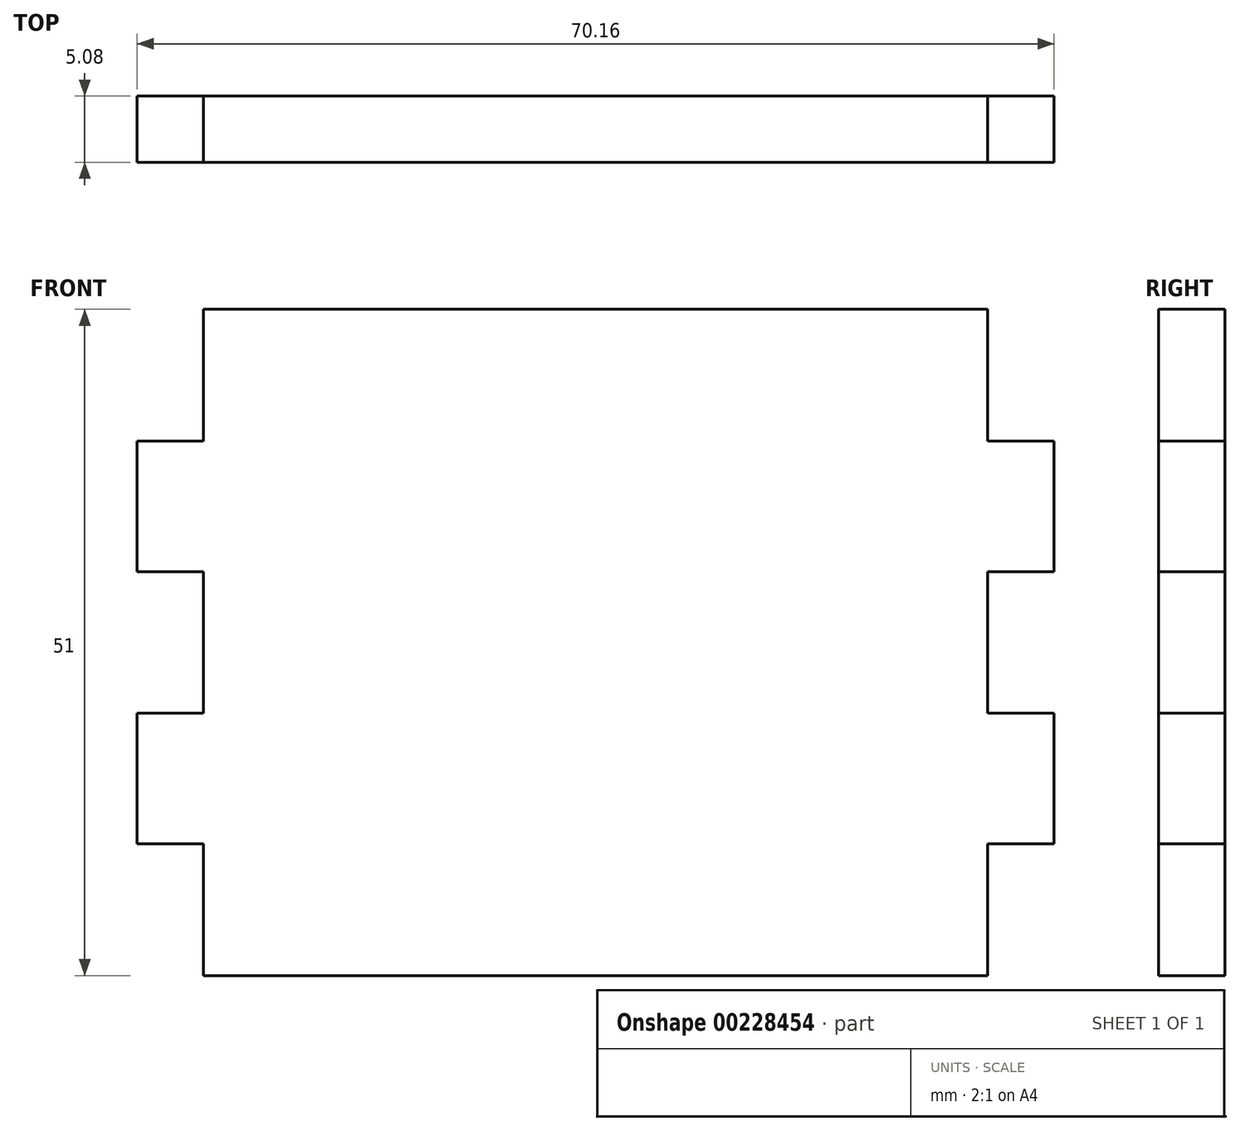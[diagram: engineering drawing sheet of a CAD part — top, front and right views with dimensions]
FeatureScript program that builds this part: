
annotation { "Feature Type Name" : "Feature", "Feature Type Description" : "" }
export const myFeature = defineFeature(function(context is Context, id is Id, definition is map)
    precondition{}
    {
        {
            var Q0;
            Q0=qCreatedBy(makeId("Front.planeOp"),FACE);
            var sketch = newSketch(context, id + "F0", { "sketchPlane" : qUnion([Q0])});
            skLineSegment(sketch, "E0.bottom", {"start": v(0, 0) * mm, "end": v(70.16, 0) * mm});
            skLineSegment(sketch, "E0.top", {"start": v(0, -51) * mm, "end": v(70.16, -51) * mm});
            skLineSegment(sketch, "E0.left", {"start": v(0, 0) * mm, "end": v(0, -51) * mm});
            skLineSegment(sketch, "E0.right", {"start": v(70.16, 0) * mm, "end": v(70.16, -51) * mm});
            skLineSegment(sketch, "E1.bottom", {"start": v(0, 0) * mm, "end": v(5.08, 0) * mm});
            skLineSegment(sketch, "E1.top", {"start": v(0, -10.1) * mm, "end": v(5.08, -10.1) * mm});
            skLineSegment(sketch, "E1.left", {"start": v(0, 0) * mm, "end": v(0, -10.1) * mm});
            skLineSegment(sketch, "E1.right", {"start": v(5.08, 0) * mm, "end": v(5.08, -10.1) * mm});
            skLineSegment(sketch, "E2.bottom", {"start": v(0, -51) * mm, "end": v(5.08, -51) * mm});
            skLineSegment(sketch, "E2.top", {"start": v(0, -40.9) * mm, "end": v(5.08, -40.9) * mm});
            skLineSegment(sketch, "E2.left", {"start": v(0, -51) * mm, "end": v(0, -40.9) * mm});
            skLineSegment(sketch, "E2.right", {"start": v(5.08, -51) * mm, "end": v(5.08, -40.9) * mm});
            skLineSegment(sketch, "E3.bottom", {"start": v(0, -20.1) * mm, "end": v(5.08, -20.1) * mm});
            skLineSegment(sketch, "E3.top", {"start": v(0, -30.9) * mm, "end": v(5.08, -30.9) * mm});
            skLineSegment(sketch, "E3.left", {"start": v(0, -20.1) * mm, "end": v(0, -30.9) * mm});
            skLineSegment(sketch, "E3.right", {"start": v(5.08, -20.1) * mm, "end": v(5.08, -30.9) * mm});
            skLineSegment(sketch, "E4", {"start": v(35.08, 52.74) * mm, "end": v(35.08, -67.4) * mm, "construction": true});
            skLineSegment(sketch, "E5.MirrorCS", {"start": v(65.08, 0) * mm, "end": v(65.08, -10.1) * mm});
            skLineSegment(sketch, "E6.MirrorCS", {"start": v(70.16, -10.1) * mm, "end": v(65.08, -10.1) * mm});
            skLineSegment(sketch, "E7.MirrorCS", {"start": v(70.16, -20.1) * mm, "end": v(65.08, -20.1) * mm});
            skLineSegment(sketch, "E8.MirrorCS", {"start": v(65.08, -20.1) * mm, "end": v(65.08, -30.9) * mm});
            skLineSegment(sketch, "E9.MirrorCS", {"start": v(70.16, -30.9) * mm, "end": v(65.08, -30.9) * mm});
            skLineSegment(sketch, "E10.MirrorCS", {"start": v(70.16, -40.9) * mm, "end": v(65.08, -40.9) * mm});
            skLineSegment(sketch, "E11.MirrorCS", {"start": v(65.08, -51) * mm, "end": v(65.08, -40.9) * mm});
            skSolve(sketch);
        }
        {
            var Q0;
            {var subQ12=sQuery(id+"F0.wireOp",EDGE,"E1.top");Q0=makeQuery(id+"F0.imprint","IMPRINT",FACE,{"disambiguationData":[TD([[makeQuery(id+"F0.imprint","IMPRINT",EDGE,{"derivedFrom":subQ12}),-1.0]])]});}
            extrude(context, id + "F1", {"entities" : qUnion([Q0]), "depth" : 5.08 * mm});
        }
    });
